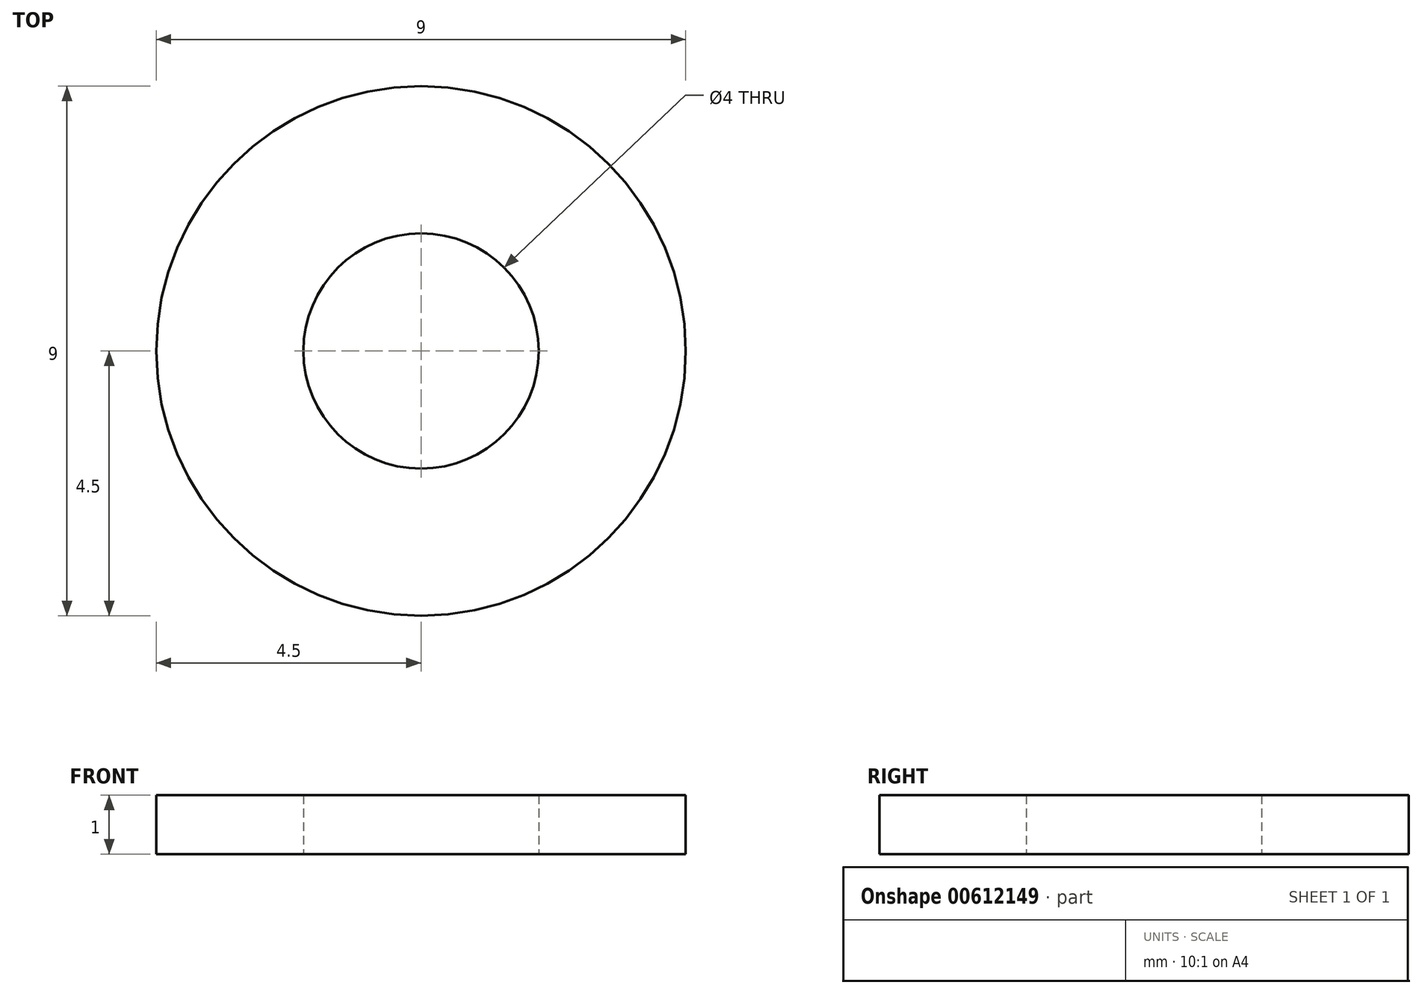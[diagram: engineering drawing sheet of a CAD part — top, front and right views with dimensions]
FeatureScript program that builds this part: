
annotation { "Feature Type Name" : "Feature", "Feature Type Description" : "" }
export const myFeature = defineFeature(function(context is Context, id is Id, definition is map)
    precondition{}
    {
        {
            var Q0;
            Q0=qCreatedBy(makeId("Top.planeOp"),FACE);
            var sketch = newSketch(context, id + "F0", { "sketchPlane" : qUnion([Q0])});
            skCircle(sketch, "E0", {"center": v(0, 0) * mm, "radius": 2 * mm});
            skPoint(sketch, "E0.first.point", {"position": v(-2, 0) * mm});
            skPoint(sketch, "E0.second.point", {"position": v(2, 0) * mm});
            skPoint(sketch, "E0.third.point", {"position": v(0, 2) * mm});
            skCircle(sketch, "E1.0", {"center": v(0, 0) * mm, "radius": 4.5 * mm});
            skSolve(sketch);
        }
        {
            var Q0;
            Q0=makeQuery(id+"F0.imprint","IMPRINT",FACE,{"disambiguationData":[TD([[makeQuery(id+"F0.imprint","IMPRINT",EDGE,{"derivedFrom":sQuery(id+"F0.wireOp",EDGE,"E0")}),-1.0]])]});
            extrude(context, id + "F1", {"entities" : qUnion([Q0]), "depth" : 1 * mm, "offsetDistance" : 25 * mm});
        }
    });
